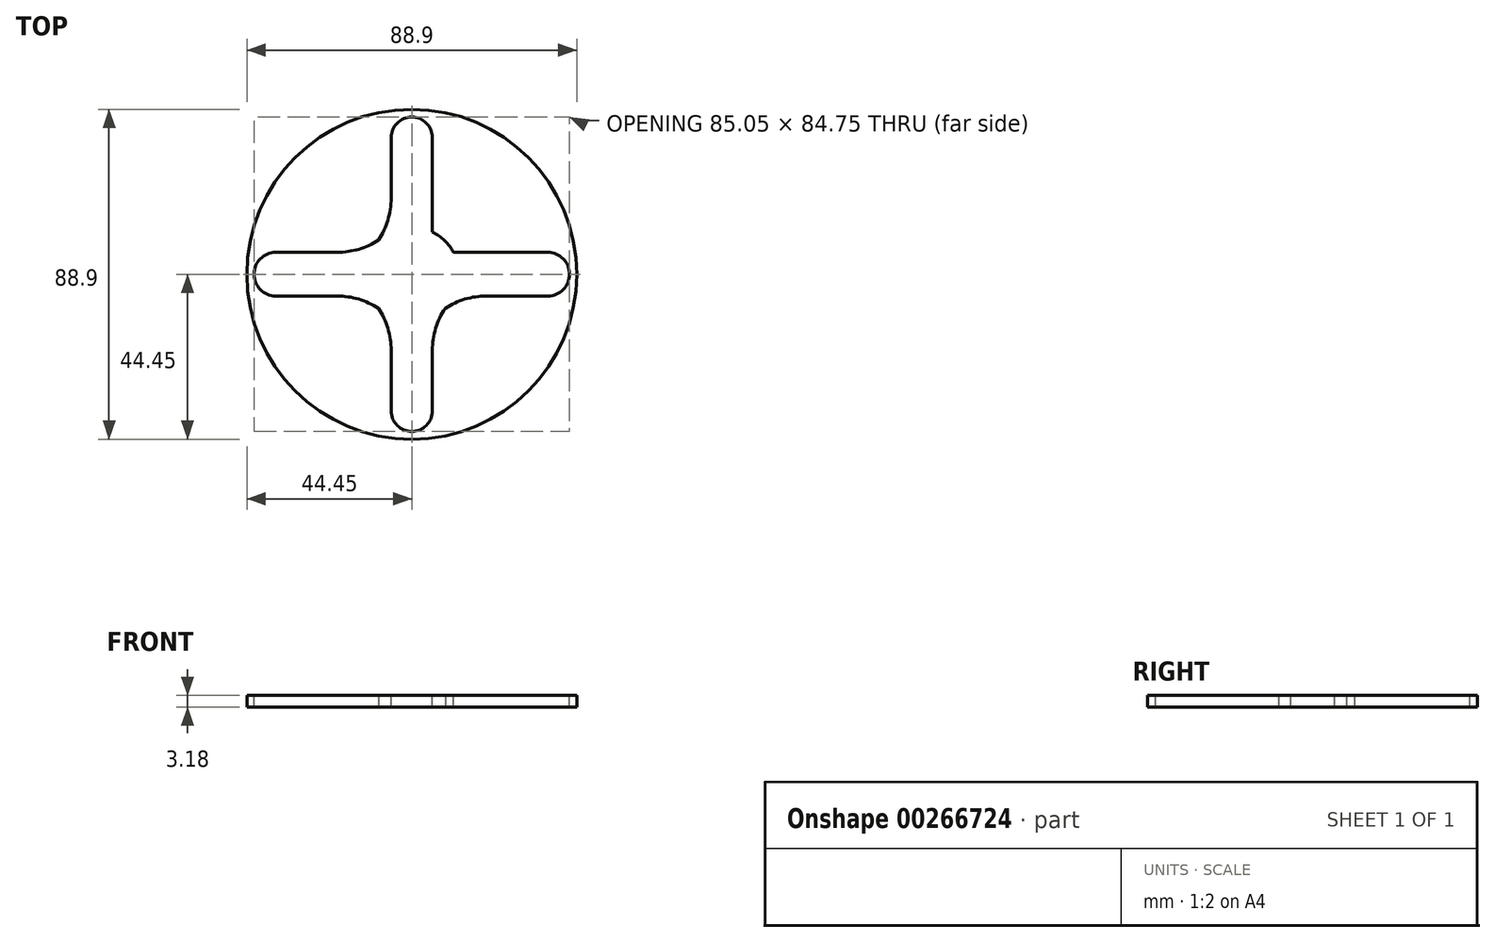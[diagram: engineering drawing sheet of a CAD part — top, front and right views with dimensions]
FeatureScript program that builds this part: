
annotation { "Feature Type Name" : "Feature", "Feature Type Description" : "" }
export const myFeature = defineFeature(function(context is Context, id is Id, definition is map)
    precondition{}
    {
        {
            var Q0;
            Q0=qCreatedBy(makeId("Top.planeOp"),FACE);
            var sketch = newSketch(context, id + "F0", { "sketchPlane" : qUnion([Q0])});
            skCircle(sketch, "E0", {"center": v(0, 0) * mm, "radius": 44.45 * mm});
            skCircle(sketch, "E1", {"center": v(0, 0) * mm, "radius": 12.7 * mm});
            skSolve(sketch);
        }
        {
            var Q0;
            Q0=makeQuery(id+"F0.imprint","IMPRINT",FACE,{"disambiguationData":[TD([[makeQuery(id+"F0.imprint","IMPRINT",EDGE,{"derivedFrom":sQuery(id+"F0.wireOp",EDGE,"E0")}),1.0]])]});
            extrude(context, id + "F1", {"entities" : qUnion([Q0]), "depth" : 3.17 * mm});
        }
        {
            var Q0;
            Q0=makeQuery(id+"F1.opExtrude","CAP_FACE",FACE,{"disambiguationData":[OSD([sQuery(id+"F0.wireOp",EDGE,"E0"),sQuery(id+"F0.wireOp",EDGE,"E1")])],"isStart":false});
            var sketch = newSketch(context, id + "F2", { "sketchPlane" : qUnion([Q0])});
            skLineSegment(sketch, "E2", {"start": v(0, 42.38) * mm, "end": v(0, -42.38) * mm});
            skLineSegment(sketch, "E3", {"start": v(42.53, 0) * mm, "end": v(-42.53, 0) * mm});
            skLineSegment(sketch, "E4", {"start": v(-11.27, -5.86) * mm, "end": v(-36.67, -5.86) * mm});
            skLineSegment(sketch, "E5", {"start": v(-11.23, 5.93) * mm, "end": v(-36.63, 5.93) * mm});
            skLineSegment(sketch, "E6.MirrorCS", {"start": v(11.27, -5.86) * mm, "end": v(36.67, -5.86) * mm});
            skLineSegment(sketch, "E7.MirrorCS", {"start": v(11.23, 5.93) * mm, "end": v(36.63, 5.93) * mm});
            skLineSegment(sketch, "E8", {"start": v(-5.56, -11.42) * mm, "end": v(-5.56, -36.82) * mm});
            skLineSegment(sketch, "E9.MirrorCS", {"start": v(5.56, -11.42) * mm, "end": v(5.56, -36.82) * mm});
            skArc(sketch, "E10", {"start": v(-5.56, -36.82) * mm, "mid": v(0, -42.38) * mm, "end": v(5.56, -36.82) * mm});
            skLineSegment(sketch, "E11.MirrorCS", {"start": v(-5.56, 11.42) * mm, "end": v(-5.56, 36.82) * mm});
            skLineSegment(sketch, "E12.MirrorCS", {"start": v(5.56, 11.42) * mm, "end": v(5.56, 36.82) * mm});
            skArc(sketch, "E13.MirrorCS", {"start": v(-5.56, 36.82) * mm, "mid": v(0, 42.38) * mm, "end": v(5.56, 36.82) * mm});
            skArc(sketch, "E14", {"start": v(36.67, -5.86) * mm, "mid": v(42.53, 0.05) * mm, "end": v(36.63, 5.93) * mm});
            skArc(sketch, "E15.MirrorCS", {"start": v(-36.67, -5.86) * mm, "mid": v(-42.53, 0.05) * mm, "end": v(-36.63, 5.93) * mm});
            skPoint(sketch, "E16.orphan", {"position": v(0, 44.45) * mm});
            skPoint(sketch, "E17.orphan", {"position": v(44.45, 0) * mm});
            skSolve(sketch);
        }
        {
            var Q0;
            {var subQ5=sQuery(id+"F2.wireOp",EDGE,"E5");Q0=makeQuery(id+"F2.imprint","IMPRINT",FACE,{"disambiguationData":[TD([[makeQuery(id+"F2.imprint","IMPRINT",EDGE,{"derivedFrom":subQ5}),1.0]])]});}
            var Q1;
            {var subQ5=sQuery(id+"F2.wireOp",EDGE,"E4");Q1=makeQuery(id+"F2.imprint","IMPRINT",FACE,{"disambiguationData":[TD([[makeQuery(id+"F2.imprint","IMPRINT",EDGE,{"derivedFrom":subQ5}),-1.0]])]});}
            var Q2;
            {var subQ5=sQuery(id+"F2.wireOp",EDGE,"E11.MirrorCS");Q2=makeQuery(id+"F2.imprint","IMPRINT",FACE,{"disambiguationData":[TD([[makeQuery(id+"F2.imprint","IMPRINT",EDGE,{"derivedFrom":subQ5}),-1.0]])]});}
            var Q3;
            {var subQ5=sQuery(id+"F2.wireOp",EDGE,"E12.MirrorCS");Q3=makeQuery(id+"F2.imprint","IMPRINT",FACE,{"disambiguationData":[TD([[makeQuery(id+"F2.imprint","IMPRINT",EDGE,{"derivedFrom":subQ5}),1.0]])]});}
            var Q4;
            {var subQ5=sQuery(id+"F2.wireOp",EDGE,"E9.MirrorCS");Q4=makeQuery(id+"F2.imprint","IMPRINT",FACE,{"disambiguationData":[TD([[makeQuery(id+"F2.imprint","IMPRINT",EDGE,{"derivedFrom":subQ5}),-1.0]])]});}
            var Q5;
            {var subQ5=sQuery(id+"F2.wireOp",EDGE,"E8");Q5=makeQuery(id+"F2.imprint","IMPRINT",FACE,{"disambiguationData":[TD([[makeQuery(id+"F2.imprint","IMPRINT",EDGE,{"derivedFrom":subQ5}),1.0]])]});}
            var Q6;
            {var subQ5=sQuery(id+"F2.wireOp",EDGE,"E7.MirrorCS");Q6=makeQuery(id+"F2.imprint","IMPRINT",FACE,{"disambiguationData":[TD([[makeQuery(id+"F2.imprint","IMPRINT",EDGE,{"derivedFrom":subQ5}),-1.0]])]});}
            var Q7;
            {var subQ5=sQuery(id+"F2.wireOp",EDGE,"E6.MirrorCS");Q7=makeQuery(id+"F2.imprint","IMPRINT",FACE,{"disambiguationData":[TD([[makeQuery(id+"F2.imprint","IMPRINT",EDGE,{"derivedFrom":subQ5}),1.0]])]});}
            extrude(context, id + "F3", {"entities" : qUnion([Q0, Q1, Q2, Q3, Q4, Q5, Q6, Q7]), "operationType" : NewBodyOperationType.REMOVE, "oppositeDirection" : true, "depth" : 25.4 * mm});
        }
        {
            var Q0;
            Q0=makeQuery(id+"F3.boolean.opBoolean","COPY",EDGE,{"derivedFrom":makeQuery(id+"F3.opExtrude","SWEPT_EDGE",EDGE,{"disambiguationData":[OSD([sQuery(id+"F0.wireOp",EDGE,"E1"),sQuery(id+"F2.wireOp",EDGE,"E8")])]})});
            var Q1;
            Q1=makeQuery(id+"F3.boolean.opBoolean","COPY",EDGE,{"derivedFrom":makeQuery(id+"F3.opExtrude","SWEPT_EDGE",EDGE,{"disambiguationData":[OSD([sQuery(id+"F0.wireOp",EDGE,"E1"),sQuery(id+"F2.wireOp",EDGE,"E4")])]})});
            var Q2;
            Q2=makeQuery(id+"F3.boolean.opBoolean","COPY",EDGE,{"derivedFrom":makeQuery(id+"F3.opExtrude","SWEPT_EDGE",EDGE,{"disambiguationData":[OSD([sQuery(id+"F0.wireOp",EDGE,"E1"),sQuery(id+"F2.wireOp",EDGE,"E7.MirrorCS")])]})});
            var Q3;
            Q3=makeQuery(id+"F3.boolean.opBoolean","COPY",EDGE,{"derivedFrom":makeQuery(id+"F3.opExtrude","SWEPT_EDGE",EDGE,{"disambiguationData":[OSD([sQuery(id+"F0.wireOp",EDGE,"E1"),sQuery(id+"F2.wireOp",EDGE,"E12.MirrorCS")])]})});
            var Q4;
            Q4=makeQuery(id+"F3.boolean.opBoolean","COPY",EDGE,{"derivedFrom":makeQuery(id+"F3.opExtrude","SWEPT_EDGE",EDGE,{"disambiguationData":[OSD([sQuery(id+"F0.wireOp",EDGE,"E1"),sQuery(id+"F2.wireOp",EDGE,"E11.MirrorCS")])]})});
            var Q5;
            Q5=makeQuery(id+"F3.boolean.opBoolean","COPY",EDGE,{"derivedFrom":makeQuery(id+"F3.opExtrude","SWEPT_EDGE",EDGE,{"disambiguationData":[OSD([sQuery(id+"F0.wireOp",EDGE,"E1"),sQuery(id+"F2.wireOp",EDGE,"E5")])]})});
            var Q6;
            Q6=makeQuery(id+"F3.boolean.opBoolean","COPY",EDGE,{"derivedFrom":makeQuery(id+"F3.opExtrude","SWEPT_EDGE",EDGE,{"disambiguationData":[OSD([sQuery(id+"F0.wireOp",EDGE,"E1"),sQuery(id+"F2.wireOp",EDGE,"E6.MirrorCS")])]})});
            var Q7;
            Q7=makeQuery(id+"F3.boolean.opBoolean","COPY",EDGE,{"derivedFrom":makeQuery(id+"F3.opExtrude","SWEPT_EDGE",EDGE,{"disambiguationData":[OSD([sQuery(id+"F0.wireOp",EDGE,"E1"),sQuery(id+"F2.wireOp",EDGE,"E9.MirrorCS")])]})});
            fillet(context, id + "F4", {"entities" : qUnion([Q0, Q1, Q2, Q3, Q4, Q5, Q6, Q7]), "radius" : 20.32 * mm, "tangentPropagation" : true, "allowEdgeOverflow" : false});
        }
    });
